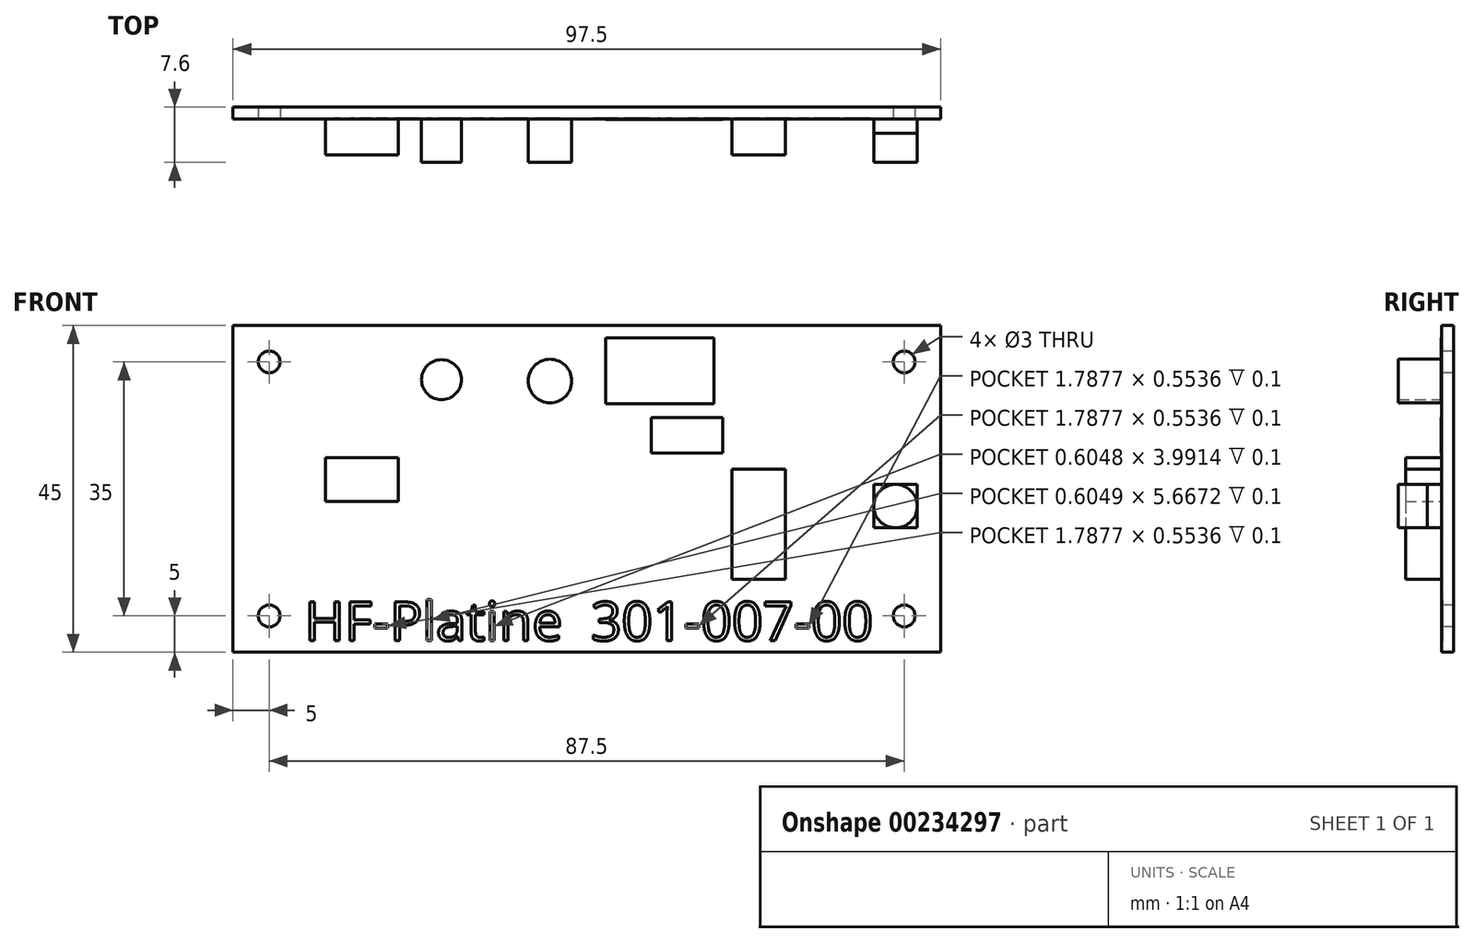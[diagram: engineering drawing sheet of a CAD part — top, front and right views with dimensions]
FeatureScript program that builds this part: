
annotation { "Feature Type Name" : "Feature", "Feature Type Description" : "" }
export const myFeature = defineFeature(function(context is Context, id is Id, definition is map)
    precondition{}
    {
        {
            var Q0;
            Q0=qCreatedBy(makeId("Front.planeOp"),FACE);
            var sketch = newSketch(context, id + "F0", { "sketchPlane" : qUnion([Q0])});
            skLineSegment(sketch, "E0.bottom", {"start": v(48.75, -22.5) * mm, "end": v(-48.75, -22.5) * mm});
            skLineSegment(sketch, "E0.top", {"start": v(48.75, 22.5) * mm, "end": v(-48.75, 22.5) * mm});
            skLineSegment(sketch, "E0.left", {"start": v(48.75, -22.5) * mm, "end": v(48.75, 22.5) * mm});
            skLineSegment(sketch, "E0.right", {"start": v(-48.75, -22.5) * mm, "end": v(-48.75, 22.5) * mm});
            skPoint(sketch, "E0.middle", {"position": v(0, 0) * mm});
            skLineSegment(sketch, "E1.bottom", {"start": v(43.75, -17.5) * mm, "end": v(-43.75, -17.5) * mm, "construction": true});
            skLineSegment(sketch, "E1.top", {"start": v(43.75, 17.5) * mm, "end": v(-43.75, 17.5) * mm, "construction": true});
            skLineSegment(sketch, "E1.left", {"start": v(43.75, -17.5) * mm, "end": v(43.75, 17.5) * mm, "construction": true});
            skLineSegment(sketch, "E1.right", {"start": v(-43.75, -17.5) * mm, "end": v(-43.75, 17.5) * mm, "construction": true});
            skCircle(sketch, "E2", {"center": v(-43.75, 17.5) * mm, "radius": 1.5 * mm});
            skCircle(sketch, "E3", {"center": v(43.75, 17.5) * mm, "radius": 1.5 * mm});
            skCircle(sketch, "E4", {"center": v(43.75, -17.5) * mm, "radius": 1.5 * mm});
            skCircle(sketch, "E5", {"center": v(-43.75, -17.5) * mm, "radius": 1.5 * mm});
            skLineSegment(sketch, "E6.bottom", {"start": v(-35.99, 4.3) * mm, "end": v(-25.99, 4.3) * mm});
            skLineSegment(sketch, "E6.top", {"start": v(-35.99, -1.7) * mm, "end": v(-25.99, -1.7) * mm});
            skLineSegment(sketch, "E6.left", {"start": v(-35.99, 4.3) * mm, "end": v(-35.99, -1.7) * mm});
            skLineSegment(sketch, "E6.right", {"start": v(-25.99, 4.3) * mm, "end": v(-25.99, -1.7) * mm});
            skLineSegment(sketch, "E7.bottom", {"start": v(20, 2.72) * mm, "end": v(27.4, 2.72) * mm});
            skLineSegment(sketch, "E7.top", {"start": v(20, -12.49) * mm, "end": v(27.4, -12.49) * mm});
            skLineSegment(sketch, "E7.left", {"start": v(20, 2.72) * mm, "end": v(20, -12.49) * mm});
            skLineSegment(sketch, "E7.right", {"start": v(27.4, 2.72) * mm, "end": v(27.4, -12.49) * mm});
            skLineSegment(sketch, "E8.bottom", {"start": v(2.6, 20.79) * mm, "end": v(17.56, 20.79) * mm});
            skLineSegment(sketch, "E8.top", {"start": v(2.6, 11.76) * mm, "end": v(17.56, 11.76) * mm});
            skLineSegment(sketch, "E8.left", {"start": v(2.6, 20.79) * mm, "end": v(2.6, 11.76) * mm});
            skLineSegment(sketch, "E8.right", {"start": v(17.56, 20.79) * mm, "end": v(17.56, 11.76) * mm});
            skCircle(sketch, "E9", {"center": v(-5.06, 14.86) * mm, "radius": 3 * mm});
            skCircle(sketch, "E10", {"center": v(-20.01, 15.05) * mm, "radius": 2.75 * mm});
            skCircle(sketch, "E11", {"center": v(42.56, -2.37) * mm, "radius": 3 * mm});
            skPoint(sketch, "E12", {"position": v(49, 0) * mm});
            skLineSegment(sketch, "E13.bottom", {"start": v(45.56, -5.37) * mm, "end": v(39.56, -5.37) * mm});
            skLineSegment(sketch, "E13.top", {"start": v(45.56, 0.63) * mm, "end": v(39.56, 0.63) * mm});
            skLineSegment(sketch, "E13.left", {"start": v(45.56, -5.37) * mm, "end": v(45.56, 0.63) * mm});
            skLineSegment(sketch, "E13.right", {"start": v(39.56, -5.37) * mm, "end": v(39.56, 0.63) * mm});
            skLineSegment(sketch, "E14.bottom", {"start": v(18.75, 4.93) * mm, "end": v(8.92, 4.93) * mm});
            skLineSegment(sketch, "E14.top", {"start": v(18.75, 9.82) * mm, "end": v(8.92, 9.82) * mm});
            skLineSegment(sketch, "E14.left", {"start": v(18.75, 4.93) * mm, "end": v(18.75, 9.82) * mm});
            skLineSegment(sketch, "E14.right", {"start": v(8.92, 4.93) * mm, "end": v(8.92, 9.82) * mm});
            skSolve(sketch);
        }
        {
            var Q0;
            Q0=makeQuery(id+"F0.imprint","IMPRINT",FACE,{"disambiguationData":[TD([[makeQuery(id+"F0.imprint","IMPRINT",EDGE,{"derivedFrom":sQuery(id+"F0.wireOp",EDGE,"E0.bottom")}),-1.0]])]});
            var Q1;
            Q1=makeQuery(id+"F0.imprint","IMPRINT",FACE,{"disambiguationData":[TD([[makeQuery(id+"F0.imprint","IMPRINT",EDGE,{"derivedFrom":sQuery(id+"F0.wireOp",EDGE,"E6.bottom")}),-1.0]])]});
            var Q2;
            Q2=makeQuery(id+"F0.imprint","IMPRINT",FACE,{"disambiguationData":[TD([[makeQuery(id+"F0.imprint","IMPRINT",EDGE,{"derivedFrom":sQuery(id+"F0.wireOp",EDGE,"E10")}),1.0]])]});
            var Q3;
            Q3=makeQuery(id+"F0.imprint","IMPRINT",FACE,{"disambiguationData":[TD([[makeQuery(id+"F0.imprint","IMPRINT",EDGE,{"derivedFrom":sQuery(id+"F0.wireOp",EDGE,"Vhg1oOLU-gX7y-QFdW-Beyx-drXknVGR0J5o.bottom")}),-1.0]])]});
            var Q4;
            Q4=makeQuery(id+"F0.imprint","IMPRINT",FACE,{"disambiguationData":[TD([[makeQuery(id+"F0.imprint","IMPRINT",EDGE,{"derivedFrom":sQuery(id+"F0.wireOp",EDGE,"E7.bottom")}),-1.0]])]});
            var Q5;
            Q5=makeQuery(id+"F0.imprint","IMPRINT",FACE,{"disambiguationData":[TD([[makeQuery(id+"F0.imprint","IMPRINT",EDGE,{"derivedFrom":sQuery(id+"F0.wireOp",EDGE,"E8.bottom")}),-1.0]])]});
            var Q6;
            Q6=makeQuery(id+"F0.imprint","IMPRINT",FACE,{"disambiguationData":[TD([[makeQuery(id+"F0.imprint","IMPRINT",EDGE,{"derivedFrom":sQuery(id+"F0.wireOp",EDGE,"E9")}),1.0]])]});
            var Q7;
            {var subQ0=sQuery(id+"F0.wireOp",EDGE,"ushDA7a9-23E1-scTQ-Ytbz-xXjpGCDGIXWz.bottom");var subQ1=sQuery(id+"F0.wireOp",EDGE,"E11");var subQ2=makeQuery(id+"F0.imprint","INTERSECT",VERTEX,{"disambiguationData":[OD(0.0)],"derivedFrom":[subQ1,subQ0]});Q7=makeQuery(id+"F0.imprint","IMPRINT",FACE,{"disambiguationData":[TD([[makeQuery(id+"F0.imprint","IMPRINT",EDGE,{"disambiguationData":[TD([[subQ2,-1.0]])],"derivedFrom":subQ1}),1.0]])]});}
            var Q8;
            {var subQ1=sQuery(id+"F0.wireOp",EDGE,"ushDA7a9-23E1-scTQ-Ytbz-xXjpGCDGIXWz.top");Q8=makeQuery(id+"F0.imprint","IMPRINT",FACE,{"disambiguationData":[TD([[makeQuery(id+"F0.imprint","IMPRINT",EDGE,{"derivedFrom":subQ1}),1.0]])]});}
            var Q9;
            {var subQ0=sQuery(id+"F0.wireOp",EDGE,"ushDA7a9-23E1-scTQ-Ytbz-xXjpGCDGIXWz.bottom");var subQ1=sQuery(id+"F0.wireOp",EDGE,"E11");var subQ2=makeQuery(id+"F0.imprint","INTERSECT",VERTEX,{"disambiguationData":[OD(0.0)],"derivedFrom":[subQ1,subQ0]});Q9=makeQuery(id+"F0.imprint","IMPRINT",FACE,{"disambiguationData":[TD([[makeQuery(id+"F0.imprint","IMPRINT",EDGE,{"disambiguationData":[TD([[subQ2,-1.0]])],"derivedFrom":subQ1}),-1.0]])]});}
            var Q10;
            {var subQ1=sQuery(id+"F0.wireOp",EDGE,"E11");var subQ9=sQuery(id+"F0.wireOp",EDGE,"E13.top");var subQ12=makeQuery(id+"F0.imprint","INTERSECT",VERTEX,{"disambiguationData":[OD(0.0)],"derivedFrom":[subQ1,subQ9]});Q10=makeQuery(id+"F0.imprint","IMPRINT",FACE,{"disambiguationData":[TD([[makeQuery(id+"F0.imprint","IMPRINT",EDGE,{"disambiguationData":[TD([[subQ12,1.0]])],"derivedFrom":subQ1}),1.0]])]});}
            var Q11;
            {var subQ0=sQuery(id+"F0.wireOp",EDGE,"E13.top");var subQ1=sQuery(id+"F0.wireOp",EDGE,"E11");var subQ2=makeQuery(id+"F0.imprint","INTERSECT",VERTEX,{"disambiguationData":[OD(1.0)],"derivedFrom":[subQ1,subQ0]});Q11=makeQuery(id+"F0.imprint","IMPRINT",FACE,{"disambiguationData":[TD([[makeQuery(id+"F0.imprint","IMPRINT",EDGE,{"disambiguationData":[TD([[subQ2,-1.0]])],"derivedFrom":subQ1}),-1.0]])]});}
            var Q12;
            {var subQ0=sQuery(id+"F0.wireOp",EDGE,"E13.right");var subQ1=sQuery(id+"F0.wireOp",EDGE,"E11");var subQ2=makeQuery(id+"F0.imprint","INTERSECT",VERTEX,{"disambiguationData":[OD(1.0)],"derivedFrom":[subQ1,subQ0]});Q12=makeQuery(id+"F0.imprint","IMPRINT",FACE,{"disambiguationData":[TD([[makeQuery(id+"F0.imprint","IMPRINT",EDGE,{"disambiguationData":[TD([[subQ2,-1.0]])],"derivedFrom":subQ1}),-1.0]])]});}
            var Q13;
            {var subQ0=sQuery(id+"F0.wireOp",EDGE,"E13.bottom");var subQ1=sQuery(id+"F0.wireOp",EDGE,"E11");var subQ2=makeQuery(id+"F0.imprint","INTERSECT",VERTEX,{"disambiguationData":[OD(1.0)],"derivedFrom":[subQ1,subQ0]});Q13=makeQuery(id+"F0.imprint","IMPRINT",FACE,{"disambiguationData":[TD([[makeQuery(id+"F0.imprint","IMPRINT",EDGE,{"disambiguationData":[TD([[subQ2,-1.0]])],"derivedFrom":subQ1}),-1.0]])]});}
            var Q14;
            {var subQ0=sQuery(id+"F0.wireOp",EDGE,"E13.top");var subQ1=sQuery(id+"F0.wireOp",EDGE,"E11");var subQ2=makeQuery(id+"F0.imprint","INTERSECT",VERTEX,{"disambiguationData":[OD(0.0)],"derivedFrom":[subQ1,subQ0]});Q14=makeQuery(id+"F0.imprint","IMPRINT",FACE,{"disambiguationData":[TD([[makeQuery(id+"F0.imprint","IMPRINT",EDGE,{"disambiguationData":[TD([[subQ2,1.0]])],"derivedFrom":subQ1}),-1.0]])]});}
            var Q15;
            Q15=makeQuery(id+"F0.imprint","IMPRINT",FACE,{"disambiguationData":[TD([[makeQuery(id+"F0.imprint","IMPRINT",EDGE,{"derivedFrom":sQuery(id+"F0.wireOp",EDGE,"E14.bottom")}),-1.0]])]});
            extrude(context, id + "F1", {"entities" : qUnion([Q0, Q1, Q2, Q3, Q4, Q5, Q6, Q7, Q8, Q9, Q10, Q11, Q12, Q13, Q14, Q15]), "oppositeDirection" : true, "depth" : 1.6 * mm, "offsetDistance" : 25 * mm});
        }
        {
            var Q0;
            Q0=makeQuery(id+"F1.opExtrude","CAP_FACE",FACE,{"disambiguationData":[OSD([sQuery(id+"F0.wireOp",EDGE,"E0.bottom"),sQuery(id+"F0.wireOp",EDGE,"E0.top"),sQuery(id+"F0.wireOp",EDGE,"E0.left"),sQuery(id+"F0.wireOp",EDGE,"E0.right"),sQuery(id+"F0.wireOp",EDGE,"E2"),sQuery(id+"F0.wireOp",EDGE,"E3"),sQuery(id+"F0.wireOp",EDGE,"E4"),sQuery(id+"F0.wireOp",EDGE,"E5")])],"isStart":true});
            var sketch = newSketch(context, id + "F2", { "sketchPlane" : qUnion([Q0])});
            skText(sketch, "E15", { "text": "HF-Platine  301-007-00", "fontName": "OpenSans-Regular.ttf"});
            const initialGuessF2  = {"E15": [-0.03889, -0.0209, 1, 0, 0.00537]};
            skSetInitialGuess(sketch, initialGuessF2);
            skSolve(sketch);
        }
        {
            var Q0;
            Q0 = qSketchRegion(id + "F2", true);
            extrude(context, id + "F3", {"entities" : qUnion([Q0]), "operationType" : NewBodyOperationType.REMOVE, "oppositeDirection" : true, "depth" : .1 * mm});
        }
        {
            var Q0;
            Q0=makeQuery(id+"F0.imprint","IMPRINT",FACE,{"disambiguationData":[TD([[makeQuery(id+"F0.imprint","IMPRINT",EDGE,{"derivedFrom":sQuery(id+"F0.wireOp",EDGE,"E8.bottom")}),-1.0]])]});
            var Q1;
            Q1=makeQuery(id+"F0.imprint","IMPRINT",FACE,{"disambiguationData":[TD([[makeQuery(id+"F0.imprint","IMPRINT",EDGE,{"derivedFrom":sQuery(id+"F0.wireOp",EDGE,"Vhg1oOLU-gX7y-QFdW-Beyx-drXknVGR0J5o.bottom")}),-1.0]])]});
            var Q2;
            Q2=makeQuery(id+"F0.imprint","IMPRINT",FACE,{"disambiguationData":[TD([[makeQuery(id+"F0.imprint","IMPRINT",EDGE,{"derivedFrom":sQuery(id+"F0.wireOp",EDGE,"E14.bottom")}),-1.0]])]});
            extrude(context, id + "F4", {"entities" : qUnion([Q0, Q1, Q2]), "operationType" : NewBodyOperationType.ADD, "depth" : .1 * mm, "offsetDistance" : 25 * mm});
        }
        {
            var Q0;
            Q0=makeQuery(id+"F0.imprint","IMPRINT",FACE,{"disambiguationData":[TD([[makeQuery(id+"F0.imprint","IMPRINT",EDGE,{"derivedFrom":sQuery(id+"F0.wireOp",EDGE,"E6.bottom")}),-1.0]])]});
            var Q1;
            Q1=makeQuery(id+"F0.imprint","IMPRINT",FACE,{"disambiguationData":[TD([[makeQuery(id+"F0.imprint","IMPRINT",EDGE,{"derivedFrom":sQuery(id+"F0.wireOp",EDGE,"E7.bottom")}),-1.0]])]});
            extrude(context, id + "F5", {"entities" : qUnion([Q0, Q1]), "operationType" : NewBodyOperationType.ADD, "depth" : 5 * mm, "offsetDistance" : 25 * mm});
        }
        {
            var Q0;
            {var subQ0=sQuery(id+"F0.wireOp",EDGE,"E13.right");var subQ1=sQuery(id+"F0.wireOp",EDGE,"E11");var subQ2=makeQuery(id+"F0.imprint","INTERSECT",VERTEX,{"derivedFrom":[subQ1,subQ0]});Q0=makeQuery(id+"F0.imprint","IMPRINT",FACE,{"disambiguationData":[TD([[makeQuery(id+"F0.imprint","IMPRINT",EDGE,{"disambiguationData":[TD([[subQ2,-1.0]])],"derivedFrom":subQ1}),-1.0]])]});}
            var Q1;
            {var subQ0=sQuery(id+"F0.wireOp",EDGE,"E13.top");var subQ1=sQuery(id+"F0.wireOp",EDGE,"E11");var subQ2=makeQuery(id+"F0.imprint","INTERSECT",VERTEX,{"derivedFrom":[subQ1,subQ0]});Q1=makeQuery(id+"F0.imprint","IMPRINT",FACE,{"disambiguationData":[TD([[makeQuery(id+"F0.imprint","IMPRINT",EDGE,{"disambiguationData":[TD([[subQ2,-1.0]])],"derivedFrom":subQ1}),-1.0]])]});}
            var Q2;
            {var subQ0=sQuery(id+"F0.wireOp",EDGE,"E13.top");var subQ1=sQuery(id+"F0.wireOp",EDGE,"E11");var subQ2=makeQuery(id+"F0.imprint","INTERSECT",VERTEX,{"derivedFrom":[subQ1,subQ0]});Q2=makeQuery(id+"F0.imprint","IMPRINT",FACE,{"disambiguationData":[TD([[makeQuery(id+"F0.imprint","IMPRINT",EDGE,{"disambiguationData":[TD([[subQ2,1.0]])],"derivedFrom":subQ1}),-1.0]])]});}
            var Q3;
            {var subQ0=sQuery(id+"F0.wireOp",EDGE,"E13.left");var subQ1=sQuery(id+"F0.wireOp",EDGE,"E11");var subQ2=makeQuery(id+"F0.imprint","INTERSECT",VERTEX,{"derivedFrom":[subQ1,subQ0]});Q3=makeQuery(id+"F0.imprint","IMPRINT",FACE,{"disambiguationData":[TD([[makeQuery(id+"F0.imprint","IMPRINT",EDGE,{"disambiguationData":[TD([[subQ2,1.0]])],"derivedFrom":subQ1}),-1.0]])]});}
            var Q4;
            {var subQ0=sQuery(id+"F0.wireOp",EDGE,"E11");var subQ1=makeQuery(id+"F0.imprint","INTERSECT",VERTEX,{"derivedFrom":[subQ0,sQuery(id+"F0.wireOp",EDGE,"E13.top")]});Q4=makeQuery(id+"F0.imprint","IMPRINT",FACE,{"disambiguationData":[TD([[makeQuery(id+"F0.imprint","IMPRINT",EDGE,{"disambiguationData":[TD([[subQ1,1.0]])],"derivedFrom":subQ0}),1.0]])]});}
            extrude(context, id + "F6", {"entities" : qUnion([Q0, Q1, Q2, Q3, Q4]), "depth" : 2 * mm, "offsetDistance" : 25 * mm});
        }
        {
            var Q0;
            {var subQ0=sQuery(id+"F0.wireOp",EDGE,"E11");var subQ1=makeQuery(id+"F0.imprint","INTERSECT",VERTEX,{"derivedFrom":[subQ0,sQuery(id+"F0.wireOp",EDGE,"E13.top")]});Q0=makeQuery(id+"F0.imprint","IMPRINT",FACE,{"disambiguationData":[TD([[makeQuery(id+"F0.imprint","IMPRINT",EDGE,{"disambiguationData":[TD([[subQ1,1.0]])],"derivedFrom":subQ0}),1.0]])]});}
            extrude(context, id + "F7", {"entities" : qUnion([Q0]), "operationType" : NewBodyOperationType.ADD, "depth" : 6 * mm, "offsetDistance" : 25 * mm});
        }
        {
            var Q0;
            Q0=makeQuery(id+"F0.imprint","IMPRINT",FACE,{"disambiguationData":[TD([[makeQuery(id+"F0.imprint","IMPRINT",EDGE,{"derivedFrom":sQuery(id+"F0.wireOp",EDGE,"E10")}),1.0]])]});
            var Q1;
            Q1=makeQuery(id+"F0.imprint","IMPRINT",FACE,{"disambiguationData":[TD([[makeQuery(id+"F0.imprint","IMPRINT",EDGE,{"derivedFrom":sQuery(id+"F0.wireOp",EDGE,"E9")}),1.0]])]});
            extrude(context, id + "F8", {"entities" : qUnion([Q0, Q1]), "operationType" : NewBodyOperationType.ADD, "depth" : 6 * mm, "offsetDistance" : 25 * mm});
        }
    });
